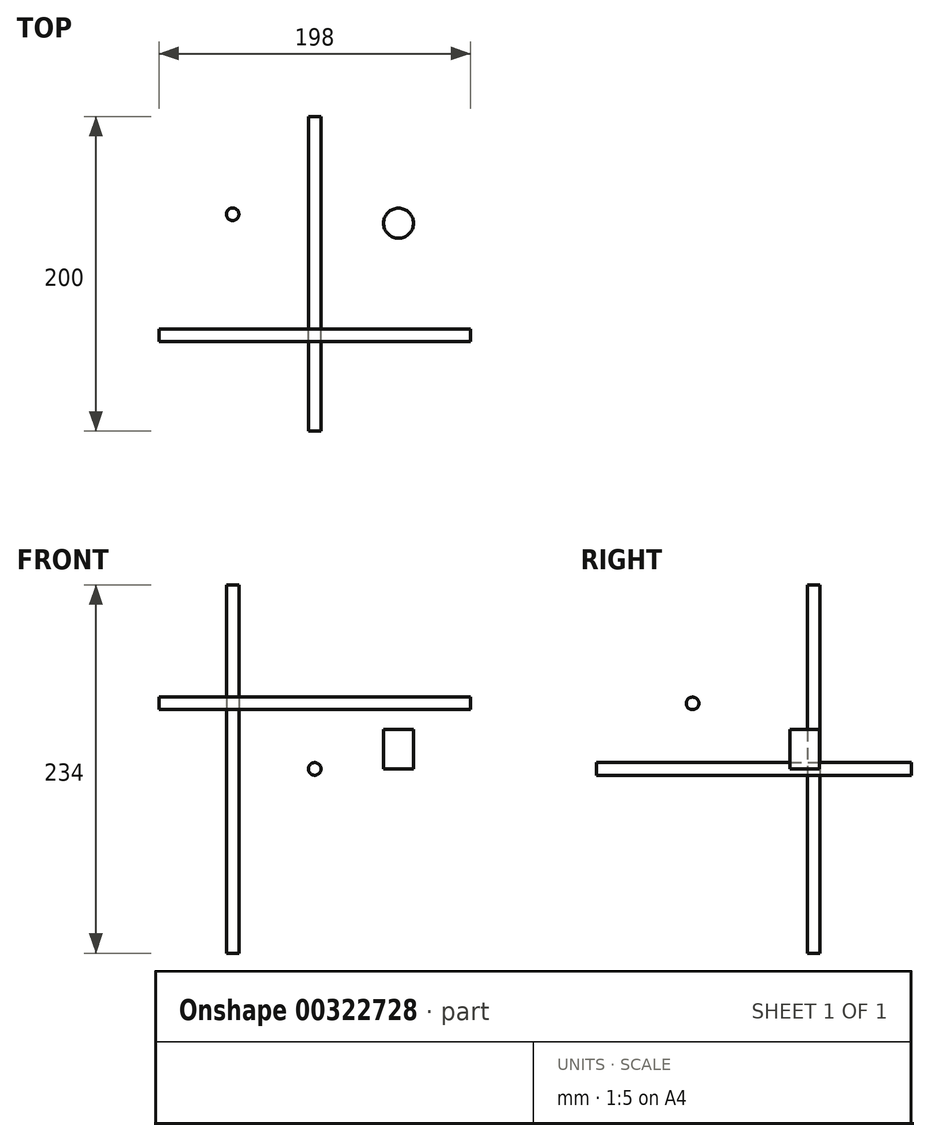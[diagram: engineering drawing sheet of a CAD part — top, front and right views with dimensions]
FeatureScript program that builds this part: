
annotation { "Feature Type Name" : "Feature", "Feature Type Description" : "" }
export const myFeature = defineFeature(function(context is Context, id is Id, definition is map)
    precondition{}
    {
        {
            var Q0;
            Q0=qCreatedBy(makeId("Front.planeOp"),FACE);
            var sketch = newSketch(context, id + "F0", { "sketchPlane" : qUnion([Q0])});
            skCircle(sketch, "E0", {"center": v(0, 0) * mm, "radius": 4 * mm});
            skSolve(sketch);
        }
        {
            var Q0;
            Q0=makeQuery(id+"F0.imprint","IMPRINT",FACE,{"disambiguationData":[TD([[makeQuery(id+"F0.imprint","IMPRINT",EDGE,{"derivedFrom":sQuery(id+"F0.wireOp",EDGE,"E0")}),1.0]])]});
            extrude(context, id + "F1", {"entities" : qUnion([Q0]), "depth" : 200 * mm, "symmetric" : true});
        }
        {
            var Q0;
            Q0=qCreatedBy(makeId("Top.planeOp"),FACE);
            var sketch = newSketch(context, id + "F2", { "sketchPlane" : qUnion([Q0])});
            skCircle(sketch, "E1", {"center": v(-52.16, 37.8) * mm, "radius": 4 * mm});
            skSolve(sketch);
        }
        {
            var Q0;
            Q0=makeQuery(id+"F2.imprint","IMPRINT",FACE,{"disambiguationData":[TD([[makeQuery(id+"F2.imprint","IMPRINT",EDGE,{"derivedFrom":sQuery(id+"F2.wireOp",EDGE,"E1")}),1.0]])]});
            extrude(context, id + "F3", {"entities" : qUnion([Q0]), "depth" : 234 * mm, "symmetric" : true});
        }
        {
            var Q0;
            Q0=qCreatedBy(makeId("Right.planeOp"),FACE);
            var sketch = newSketch(context, id + "F4", { "sketchPlane" : qUnion([Q0])});
            skCircle(sketch, "E2", {"center": v(-39.06, 41.64) * mm, "radius": 4 * mm});
            skSolve(sketch);
        }
        {
            var Q0;
            Q0=makeQuery(id+"F4.imprint","IMPRINT",FACE,{"disambiguationData":[TD([[makeQuery(id+"F4.imprint","IMPRINT",EDGE,{"derivedFrom":sQuery(id+"F4.wireOp",EDGE,"E2")}),1.0]])]});
            extrude(context, id + "F5", {"entities" : qUnion([Q0]), "depth" : 198 * mm, "symmetric" : true});
        }
        {
            var Q0;
            Q0=qCreatedBy(makeId("Top.planeOp"),FACE);
            var sketch = newSketch(context, id + "F6", { "sketchPlane" : qUnion([Q0])});
            skCircle(sketch, "E3", {"center": v(53.2, 32.14) * mm, "radius": 9.5 * mm});
            skSolve(sketch);
        }
        {
            var Q0;
            Q0 = qSketchRegion(id + "F6", true);
            extrude(context, id + "F7", {"entities" : qUnion([Q0]), "depth" : 25 * mm, "offsetDistance" : 25 * mm});
        }
    });
